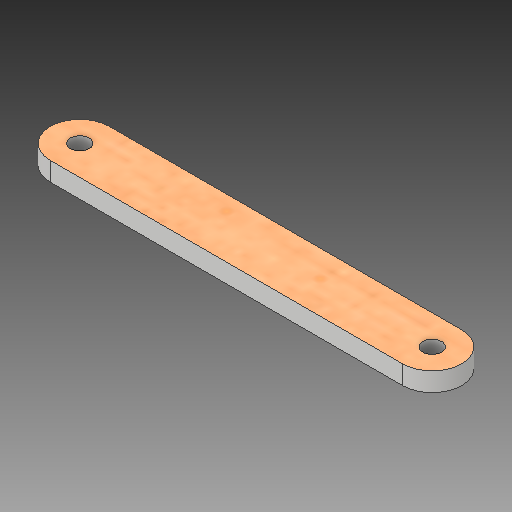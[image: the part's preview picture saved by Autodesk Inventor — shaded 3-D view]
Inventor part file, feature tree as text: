
AUTODESK INVENTOR PART (.ipt)
format: ipt  version: 2018 (Build 220112000, 112)  size: 115,712 bytes
history: native  units: mm
features: extrude x1, sketch x1
ambient origin geometry x8: Origin, YZ Plane, XZ Plane, XY Plane, X Axis, Y Axis, Z Axis, Center Point
bodies: Solid1 (feature_tree)
feature tree (2):
  extrude  "Extrusion1"  Depth=3.2mm
  sketch  "Sketch1"  dims[d0=3.2mm d1=3.2mm d2=59.755753mm d5=3.2mm d6=0.0mm d12=10.0mm d13=10.0mm]
